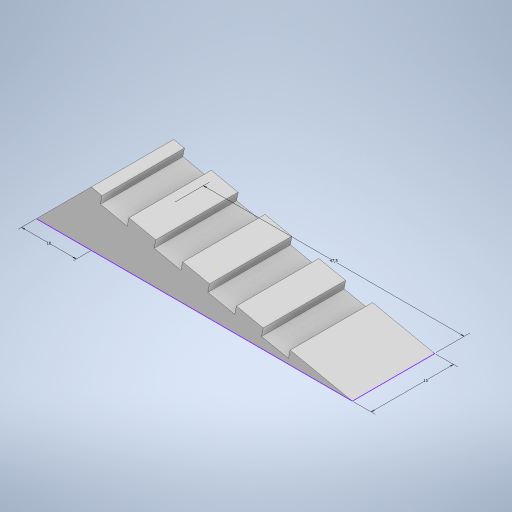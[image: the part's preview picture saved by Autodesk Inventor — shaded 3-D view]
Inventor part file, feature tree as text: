
AUTODESK INVENTOR PART (.ipt)
format: ipt  version: 2023.1 (Build 271208000, 208)  size: 286,720 bytes
history: native  units: mm
features: sketch x5, extrude x5
ambient origin geometry x8: Origin, YZ Plane, XZ Plane, XY Plane, X Axis, Y Axis, Z Axis, Center Point
bodies: Volumenkörper1 (feature_tree)
feature tree (10):
  sketch  "Skizze1"  dims[d0=47.5mm d1=15.0mm]
  extrude  "Extrusion1"  Depth=15.0mm
  extrude  "Extrusion2"  Depth=10.0mm TaperAngle=0.0deg
  sketch  "Skizze3"  dims[d6=10.0mm d7=10.0mm d8=0.0mm]
  extrude  "Extrusion3"  Depth=10.0mm TaperAngle=0.0deg
  extrude  "Extrusion4"  Depth=5.0mm
  extrude  "Extrusion5"  Depth=10.0mm
  sketch  "Skizze2"  dims[d2=10.0mm d3=0.0mm d4=10.0mm d5=0.0mm]
  sketch  "Skizze6"  dims[d9=15.0mm d10=0.0mm d11=5.0mm]
  sketch  "Skizze7"  dims[d12=2.0mm d13=40.0mm d15=10.0mm d16=10.0mm d18=10.0mm d20=1.5mm d21=0.0mm]
